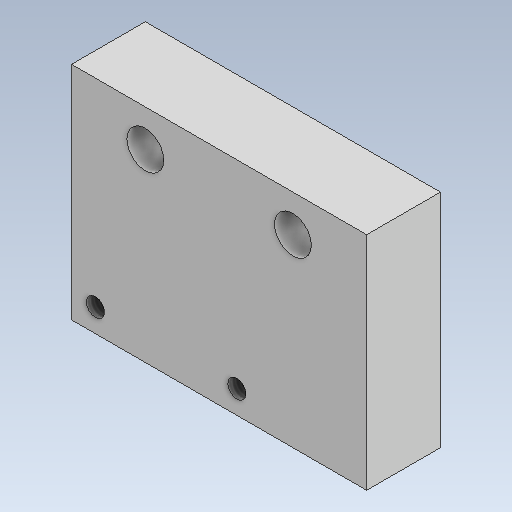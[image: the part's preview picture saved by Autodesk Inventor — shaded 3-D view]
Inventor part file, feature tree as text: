
AUTODESK INVENTOR PART (.ipt)
format: ipt  version: 2020 (Build 240168000, 168)  size: 113,664 bytes
history: native  units: mm
features: sketch x3, other x3, hole x2, reference x2, extrude x1
ambient origin geometry x8: Origin, YZ Plane, XZ Plane, XY Plane, X Axis, Y Axis, Z Axis, Center Point
bodies: Solid1 (feature_tree)
feature tree (11):
  extrude  "Extrusion1"  Depth=30.0mm
  hole  "Hole1"  [1 undecoded]
  hole  "Hole2"  [1 undecoded]
  sketch  "Sketch1"  dims[d0=40.0mm d1=30.0mm]
  sketch  "Sketch2"  dims[d2=10.0mm d3=0.0mm d4=5.0mm]
  sketch  "Sketch3"  dims[d5=10.0mm d6=10.0mm d7=5.0mm d8=6.0mm d9=12.0mm d10=2.0mm d11=90.0deg d12=8.0mm d13=20.594885mm d14=2.459mm d15=6.0mm d16=4.0mm d17=2.0mm d18=90.0deg d19=8.0mm d20=20.594885mm]
  reference  "Reference1"
  reference  "Reference2"
  parser-record x1  (decoder bookkeeping rows leaked as tree rows — omitted from the tree; the rows remain in map.json)
  other  "0008-10-04 Z axis.iam"
  other  "0008-20-1003 Switch:2"
note: 2 required parameter values undecoded (feature->parameter linkage not recoverable at this tier; creation-order binding heuristic only, values carry confidence <= 0.55)
note: 1 file-system path scrubbed to <path> (originals preserved in map.json)
